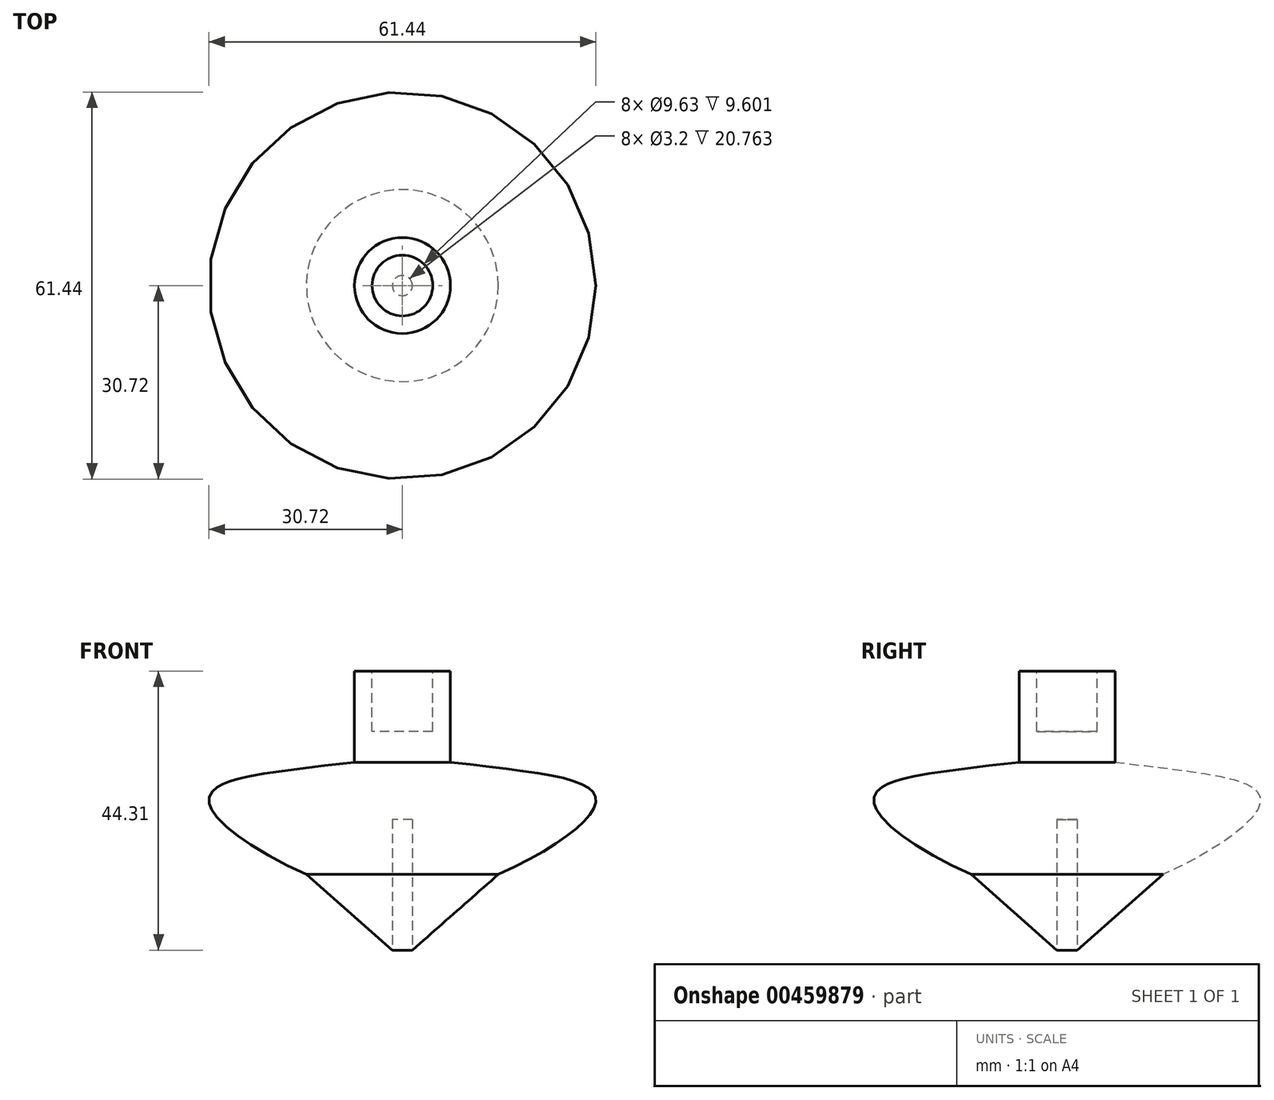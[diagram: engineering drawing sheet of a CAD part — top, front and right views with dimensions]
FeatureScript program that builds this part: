
annotation { "Feature Type Name" : "Feature", "Feature Type Description" : "" }
export const myFeature = defineFeature(function(context is Context, id is Id, definition is map)
    precondition{}
    {
        {
            var Q0;
            Q0=qCreatedBy(makeId("Front.planeOp"),FACE);
            var sketch = newSketch(context, id + "F0", { "sketchPlane" : qUnion([Q0])});
            skLineSegment(sketch, "E0", {"start": v(7.62, 31.25) * mm, "end": v(7.62, 45.72) * mm});
            skLineSegment(sketch, "E1", {"start": v(0, 45.72) * mm, "end": v(7.62, 45.72) * mm});
            skLineSegment(sketch, "E2", {"start": v(0, 45.72) * mm, "end": v(0, 0) * mm});
            skFitSpline(sketch, "E3", {"points": [v(15.24, 13.44) * mm, v(30.67, 25.73) * mm, v(7.62, 31.25) * mm], "startDerivative": vector(61.07, 27.17) * mm, "endDerivative": vector(-73.96, 8.77) * mm});
            skLineSegment(sketch, "E4", {"start": v(0, 0) * mm, "end": v(0, 0) * mm});
            skLineSegment(sketch, "E5", {"start": v(0, 0) * mm, "end": v(15.24, 13.44) * mm});
            skSolve(sketch);
        }
        {
            var Q0;
            Q0 = qSketchRegion(id + "F0", true);
            var Q1;
            Q1=sQuery(id+"F0.wireOp",EDGE,"E2");
            revolve(context, id + "F1", {"entities" : qUnion([Q0]), "axis" : qUnion([Q1]), "revolveType" : RevolveType.FULL});
        }
        {
            var Q0;
            Q0=makeQuery(id+"F1.opRevolve","SWEPT_FACE",FACE,{"disambiguationData":[OSD([sQuery(id+"F0.wireOp",EDGE,"E1")])]});
            var sketch = newSketch(context, id + "F2", { "sketchPlane" : qUnion([Q0])});
            skCircle(sketch, "E6", {"center": v(0, 0) * mm, "radius": 4.81 * mm});
            skSolve(sketch);
        }
        {
            var Q0;
            Q0 = qSketchRegion(id + "F2", true);
            extrude(context, id + "F3", {"entities" : qUnion([Q0]), "operationType" : NewBodyOperationType.REMOVE, "oppositeDirection" : true, "depth" : 9.6 * mm});
        }
        {
            var Q0;
            Q0=qCreatedBy(makeId("Top.planeOp"),FACE);
            var sketch = newSketch(context, id + "F4", { "sketchPlane" : qUnion([Q0])});
            skCircle(sketch, "E7", {"center": v(0, 0) * mm, "radius": 1.6 * mm});
            skSolve(sketch);
        }
        {
            var Q0;
            Q0 = qSketchRegion(id + "F4", true);
            extrude(context, id + "F5", {"entities" : qUnion([Q0]), "operationType" : NewBodyOperationType.REMOVE, "depth" : 22.17 * mm});
        }
    });
